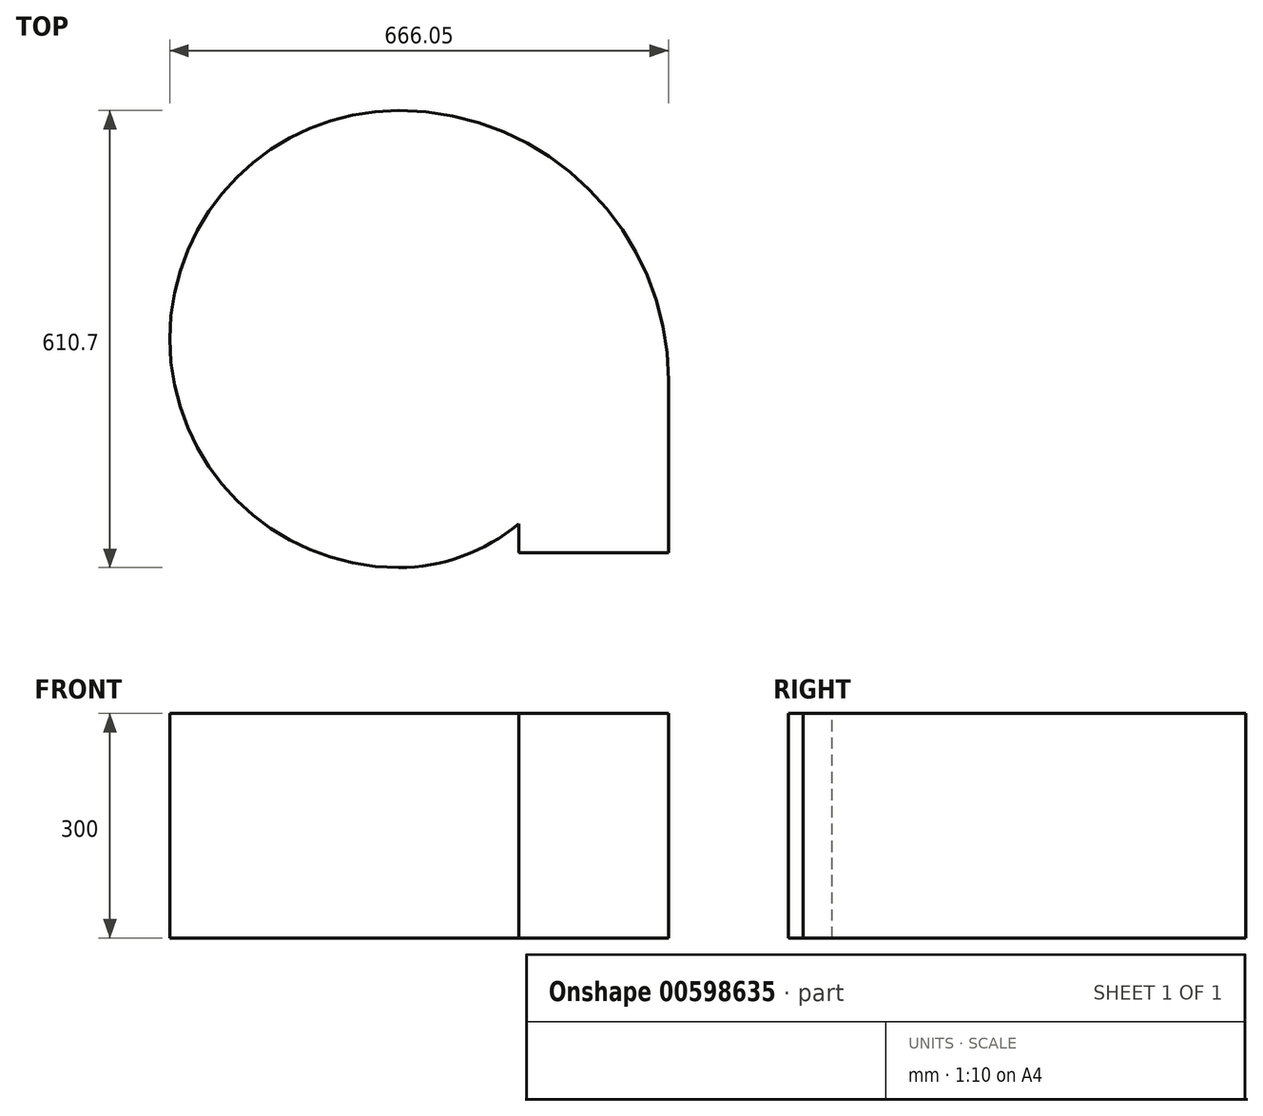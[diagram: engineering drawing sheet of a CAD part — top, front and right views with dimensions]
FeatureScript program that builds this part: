
annotation { "Feature Type Name" : "Feature", "Feature Type Description" : "" }
export const myFeature = defineFeature(function(context is Context, id is Id, definition is map)
    precondition{}
    {
        {
            var Q0;
            Q0=qCreatedBy(makeId("Top.planeOp"),FACE);
            var sketch = newSketch(context, id + "F0", { "sketchPlane" : qUnion([Q0])});
            skArc(sketch, "E0", {"start": v(0, -250) * mm, "mid": v(85.5, -234.92) * mm, "end": v(160.7, -191.51) * mm});
            skLineSegment(sketch, "E1", {"start": v(0, -176.78) * mm, "end": v(0, -176.78) * mm});
            skLineSegment(sketch, "E2", {"start": v(0, -250) * mm, "end": v(0, 0) * mm, "construction": true});
            skLineSegment(sketch, "E3", {"start": v(0, 0) * mm, "end": v(250, 0) * mm, "construction": true});
            skLineSegment(sketch, "E4", {"start": v(0, 0) * mm, "end": v(160.7, -191.51) * mm, "construction": true});
            skLineSegment(sketch, "E5", {"start": v(160.7, -230) * mm, "end": v(160.7, -191.51) * mm});
            skPoint(sketch, "E6.orphan", {"position": v(0, 88.7) * mm});
            skLineSegment(sketch, "E7", {"start": v(360.7, -230) * mm, "end": v(160.7, -230) * mm});
            skPoint(sketch, "E8.start.orphan", {"position": v(250, 194.1) * mm});
            skLineSegment(sketch, "E9", {"start": v(260.7, 0) * mm, "end": v(260.7, -230) * mm, "construction": true});
            skLineSegment(sketch, "E10", {"start": v(360.7, 0) * mm, "end": v(360.7, -230) * mm});
            skArc(sketch, "E11", {"start": v(360.7, 0) * mm, "mid": v(255.05, 255.05) * mm, "end": v(0, 360.7) * mm});
            skLineSegment(sketch, "E12", {"start": v(0, 360.7) * mm, "end": v(0, 0) * mm});
            skPoint(sketch, "E13.orphan", {"position": v(0, 838) * mm});
            skArc(sketch, "E14", {"start": v(0, 360.7) * mm, "mid": v(-305.35, 55.35) * mm, "end": v(0, -250) * mm});
            skSolve(sketch);
        }
        {
            var Q0;
            Q0=makeQuery(id+"F0.imprint","IMPRINT",FACE,{"disambiguationData":[TD([[makeQuery(id+"F0.imprint","IMPRINT",EDGE,{"derivedFrom":sQuery(id+"F0.wireOp",EDGE,"E0")}),1.0]])]});
            extrude(context, id + "F1", {"entities" : qUnion([Q0]), "oppositeDirection" : true, "depth" : 300 * mm, "offsetDistance" : 25 * mm});
        }
    });
